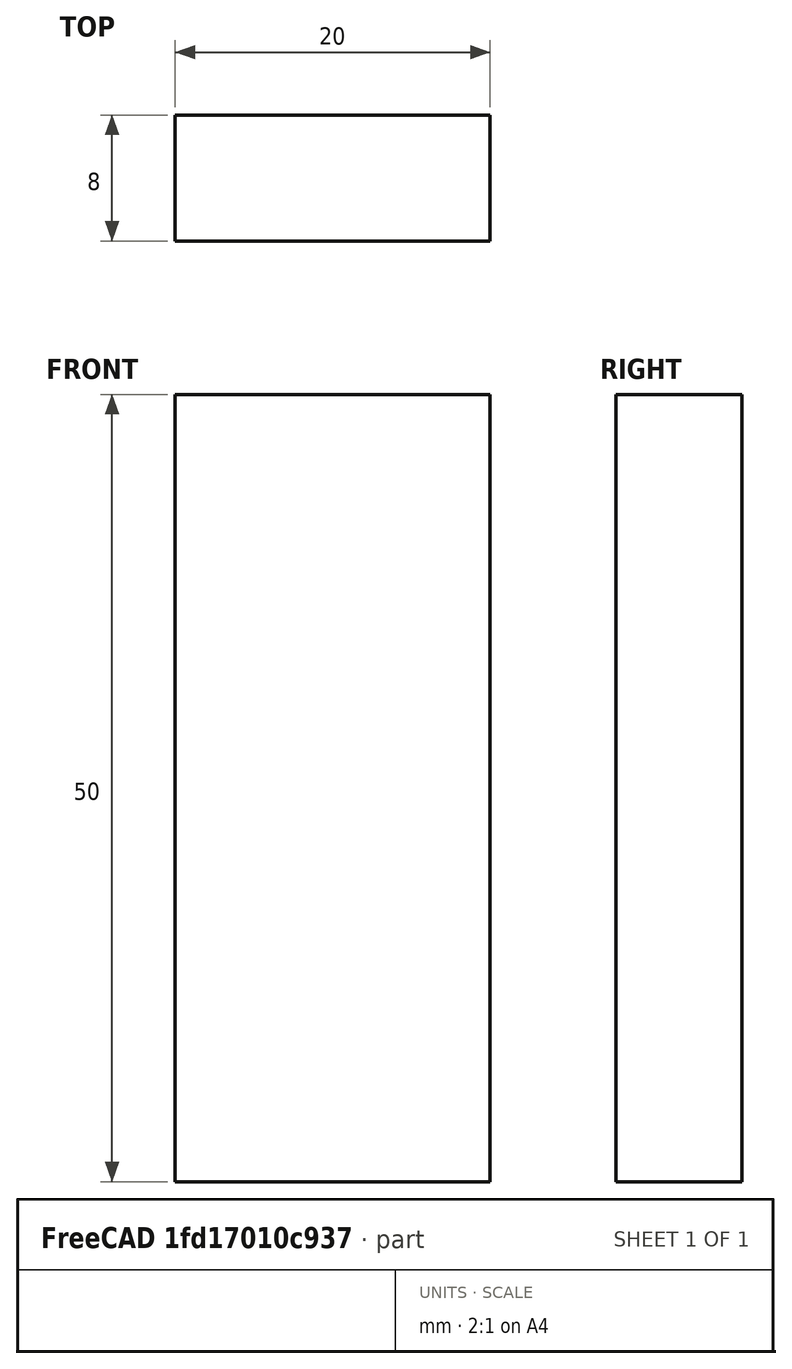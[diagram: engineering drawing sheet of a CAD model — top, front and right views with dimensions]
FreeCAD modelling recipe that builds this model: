
FCSTD DOCUMENT  (FreeCAD 0.15R4671 (Git))
Label: Flat Bar 20x8 EN10058 S235JR
License: All rights reserved
LicenseURL: http://en.wikipedia.org/wiki/All_rights_reserved
objects: Sketcher::SketchObject×1, Part::Extrusion×1
note: 2 computed .brp shape members not serialized (recipe doc carries the construction recipe); baked Part::Feature solids carry a one-line shape summary decoded from their .brp

FEATURE [Sketcher::SketchObject] Sketch
  sketch-geometry (4):
    g0: LineSegment StartX=-10 StartY=-4 StartZ=0 EndX=10 EndY=-4 EndZ=0
    g1: LineSegment StartX=10 StartY=-4 StartZ=0 EndX=10 EndY=4 EndZ=0
    g2: LineSegment StartX=10 StartY=4 StartZ=0 EndX=-10 EndY=4 EndZ=0
    g3: LineSegment StartX=-10 StartY=4 StartZ=0 EndX=-10 EndY=-4 EndZ=0
  constraints (12):
    c: Coincident(g0,g1)
    c: Coincident(g1,g2)
    c: Coincident(g2,g3)
    c: Coincident(g3,g0)
    c: Horizontal(g0)
    c: Horizontal(g2)
    c: Vertical(g1)
    c: Vertical(g3)
    c: Symmetric(g1,g2,g-2)
    c: Symmetric(g0,g1,g-1)
    c: DistanceY(g1) = 8
    c: DistanceX(g0) = 20
FEATURE [Part::Extrusion] Extrude  label="Flat Bar 20x8 EN10058 S235JR"
  Base = -> Sketch
  Dir = (0,0,50)
  Solid = true
